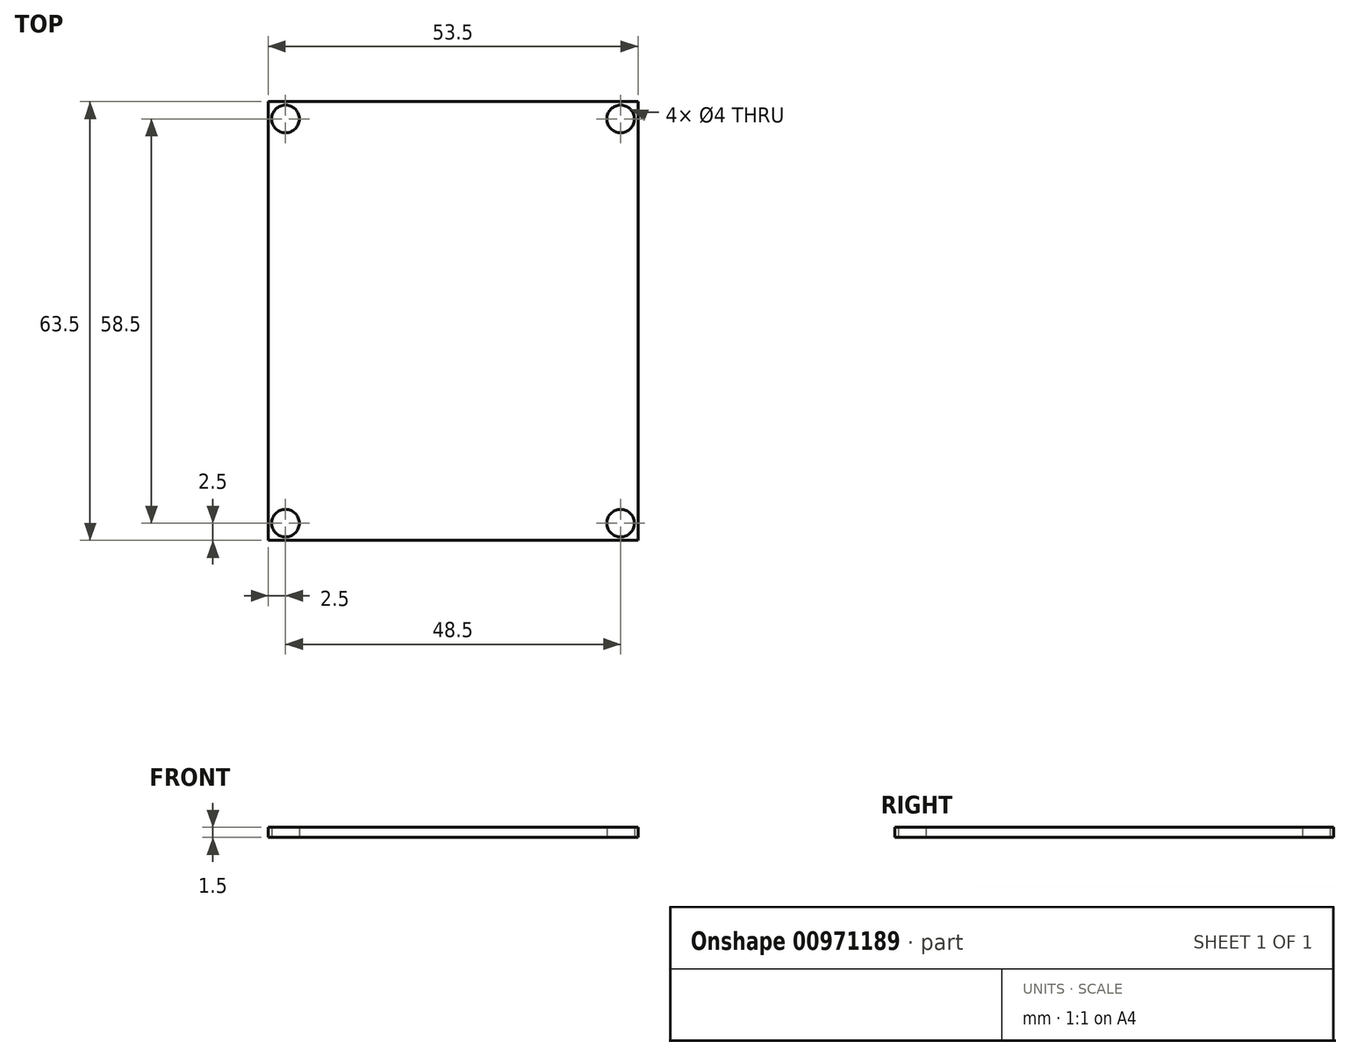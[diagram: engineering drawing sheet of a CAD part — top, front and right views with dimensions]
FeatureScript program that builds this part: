
annotation { "Feature Type Name" : "Feature", "Feature Type Description" : "" }
export const myFeature = defineFeature(function(context is Context, id is Id, definition is map)
    precondition{}
    {
        {
            var Q0;
            Q0=qCreatedBy(makeId("Top.planeOp"),FACE);
            var sketch = newSketch(context, id + "F0", { "sketchPlane" : qUnion([Q0])});
            skLineSegment(sketch, "E0.bottom", {"start": v(0, 0) * mm, "end": v(53.5, 0) * mm});
            skLineSegment(sketch, "E0.top", {"start": v(0, 63.5) * mm, "end": v(53.5, 63.5) * mm});
            skLineSegment(sketch, "E0.left", {"start": v(0, 0) * mm, "end": v(0, 63.5) * mm});
            skLineSegment(sketch, "E0.right", {"start": v(53.5, 0) * mm, "end": v(53.5, 63.5) * mm});
            skCircle(sketch, "E1", {"center": v(2.5, 61) * mm, "radius": 2 * mm});
            skCircle(sketch, "E2", {"center": v(51, 61) * mm, "radius": 2 * mm});
            skCircle(sketch, "E3", {"center": v(2.5, 2.5) * mm, "radius": 2 * mm});
            skCircle(sketch, "E4", {"center": v(51, 2.5) * mm, "radius": 2 * mm});
            skSolve(sketch);
        }
        {
            var Q0;
            Q0=makeQuery(id+"F0.imprint","IMPRINT",FACE,{"disambiguationData":[TD([[makeQuery(id+"F0.imprint","IMPRINT",EDGE,{"derivedFrom":sQuery(id+"F0.wireOp",EDGE,"E0.bottom")}),1.0]])]});
            extrude(context, id + "F1", {"entities" : qUnion([Q0]), "depth" : 1.5 * mm, "offsetDistance" : 25 * mm});
        }
    });
